# Revit family: Kombiprofilhalter
name_source: partatom
category: HLS-Bauteile
revit_build: Autodesk Revit 2018 (Build: 20190510_1515(x64)
units: mm (PartAtom-declared; Revit-internal decimal feet)

## family parameters
Arbeitsebenenbasiert = Ja
Beim Laden mit Abzugskörper schneiden = Nein
Bemaßung runder Anschluss = Durchmesser verwenden
Gemeinsam genutzt = Ja
Immer vertikal = Nein
Raumberechnungspunkt = Nein
Teiletyp = Normal

## types (3) — shared parameters
Fabrikat = MEFA
Firma = MEFA Befestigungs- und Montagesysteme GmbH
Gewicht = 0.05 kg
Gewicht pro Bauteil = 0.05 kg
Höhe = 10.1 mm
Kurztext1 = Kombiprofilhalter
Länge = 52 mm
Material = Stahl
Materialname = S235
Mengeneinheit = St
Oberflaeche = galvanisch verzinkt
Profiltyp = 35, 45, Stex 35
Stärke Material = 3 mm  [stored 0.00984252 ft]
Vorgabe-Ansicht = 1219 mm
max. zul. Last = 4.70 kN
vpe = 100 St

## per-type parameters (varying)
| type | Artikelnummer | D | EAN | Kurztext2 | Lochdurchmesser |
| Kombiprofilhalter 11 | 08095035 | 11 mm  [stored 0.0360892 ft] | 4250928419330 | Bohrung 11 mm für Gewinde M10 | 11 mm |
| Kombiprofilhalter 13 | 08162945 | 13 mm | 4250928420282 | Bohrung 13 mm für Gewinde M12 | 13 mm |
| Kombiprofilhalter 17 | 08163365 | 17 mm | 4250928420299 | Bohrung 17 mm für Gewinde M16 | 17 mm |

note: [stored X ft] marks values corroborated as IEEE doubles in the binary element streams (Revit-internal decimal feet)
